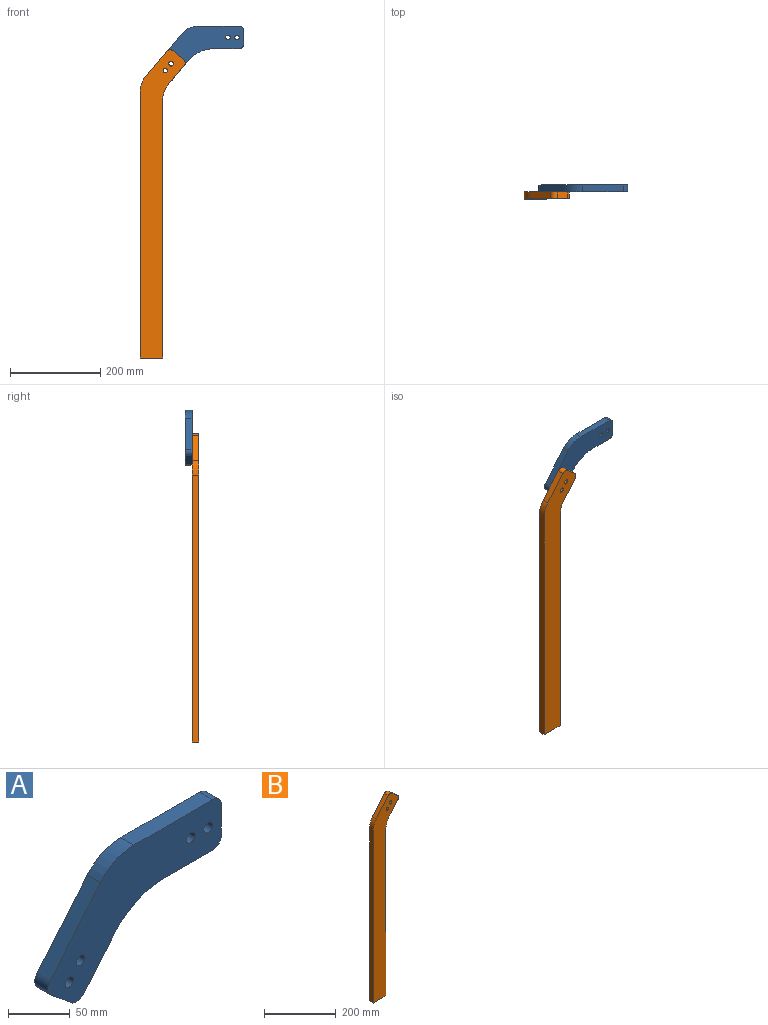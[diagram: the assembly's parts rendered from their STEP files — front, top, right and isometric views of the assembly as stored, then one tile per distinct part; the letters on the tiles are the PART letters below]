
ASSEMBLY  parts=2 mates=1
PART A: 18 faces, bbox 198.5x15x122.5 mm
  f0: plane 22.98x19.28mm, normal (-0.64,0,-0.77), area 450mm2, adj f1,f11,f12,f13
  f1: cylinder r=10mm len=15mm, axis (0,-1,0), area 235.6mm2, adj f0,f2,f12,f13
  f2: plane 42.15x35.37mm, normal (0.77,0,-0.64), area 825.4mm2, adj f1,f3,f12,f13
  f3: cylinder r=75mm len=57.45mm, axis (0,-1,0), area 981.7mm2, adj f2,f4,f12,f13
  f4: plane 55.03x15mm, normal (0,0,-1), area 825.4mm2, adj f3,f5,f12,f13
  f5: cylinder r=10mm len=15mm, axis (0,-1,0), area 235.6mm2, adj f4,f6,f12,f13
  f6: plane 30x15mm, normal (1,0,0), area 450mm2, adj f5,f7,f12,f13
  f7: cylinder r=10mm len=15mm, axis (0,-1,0), area 235.6mm2, adj f6,f8,f12,f13
  f8: plane 90x15mm, normal (0,0,1), area 1350mm2, adj f7,f9,f12,f13
  f9: cylinder r=50mm len=38.3mm, axis (0,-1,0), area 654.5mm2, adj f8,f10,f12,f13
  f10: plane 68.94x57.85mm, normal (-0.77,0,0.64), area 1350mm2, adj f9,f11,f12,f13
  f11: cylinder r=10mm len=15mm, axis (0,-1,0), area 235.6mm2, adj f0,f10,f12,f13
  f12: plane 198.49x122.52mm, normal (0,1,0), area 10859.4mm2, adj f0,f1,f2,f3,f4,f5,f6,f7
  f13: plane 198.49x122.52mm, normal (0,-1,0), area 10859.4mm2, adj f0,f1,f2,f3,f4,f5,f6,f7
  f14: cylinder r=5mm len=15mm, axis (0,1,0), area 471.2mm2, adj f12,f13
  f15: cylinder r=5mm len=15mm, axis (0,1,0), area 471.2mm2, adj f12,f13
  f16: cylinder r=5mm len=15mm, axis (0,1,0), area 471.2mm2, adj f12,f13
  f17: cylinder r=5mm len=15mm, axis (0,1,0), area 471.2mm2, adj f12,f13
PART B: 14 faces, bbox 99.4x15x682.4 mm
  f0: cylinder r=10mm len=15mm, axis (0,1,0), area 235.6mm2, adj f1,f9,f10,f11
  f1: plane 56.07x47.05mm, normal (-0.77,0,0.64), area 1098mm2, adj f0,f2,f10,f11
  f2: cylinder r=50mm len=32.14mm, axis (0,1,0), area 523.6mm2, adj f1,f3,f10,f11
  f3: plane 590.62x15mm, normal (-1,0,0), area 8859.4mm2, adj f2,f4,f10,f11
  f4: plane 50x15mm, normal (0,0,-1), area 750mm2, adj f3,f5,f10,f11
  f5: plane 572.43x15mm, normal (1,0,0), area 8586.4mm2, adj f4,f6,f10,f11
  f6: cylinder r=50mm len=32.14mm, axis (0,1,0), area 523.6mm2, adj f5,f7,f10,f11
  f7: plane 42.13x35.35mm, normal (0.77,0,-0.64), area 825mm2, adj f6,f8,f10,f11
  f8: cylinder r=10mm len=15mm, axis (0,1,0), area 235.6mm2, adj f7,f9,f10,f11
  f9: plane 22.98x19.28mm, normal (0.64,0,0.77), area 450mm2, adj f0,f8,f10,f11
  f10: plane 682.41x99.39mm, normal (0,-1,0), area 34401.1mm2, adj f0,f1,f2,f3,f4,f5,f6,f7
  f11: plane 682.41x99.39mm, normal (0,1,0), area 34401.1mm2, adj f0,f1,f2,f3,f4,f5,f6,f7
  f12: cylinder r=5mm len=15mm, axis (0,1,0), area 471.2mm2, adj f10,f11
  f13: cylinder r=5mm len=15mm, axis (0,1,0), area 471.2mm2, adj f10,f11
PLACE A t=(153.13,-11.02,119.17)mm
PLACE B t=(153.13,-11.02,119.17)mm
MATE fastened A.f14 <-> B.f12  axis (0,-1,0) through (-270.66,-292.27,20.12)mm
